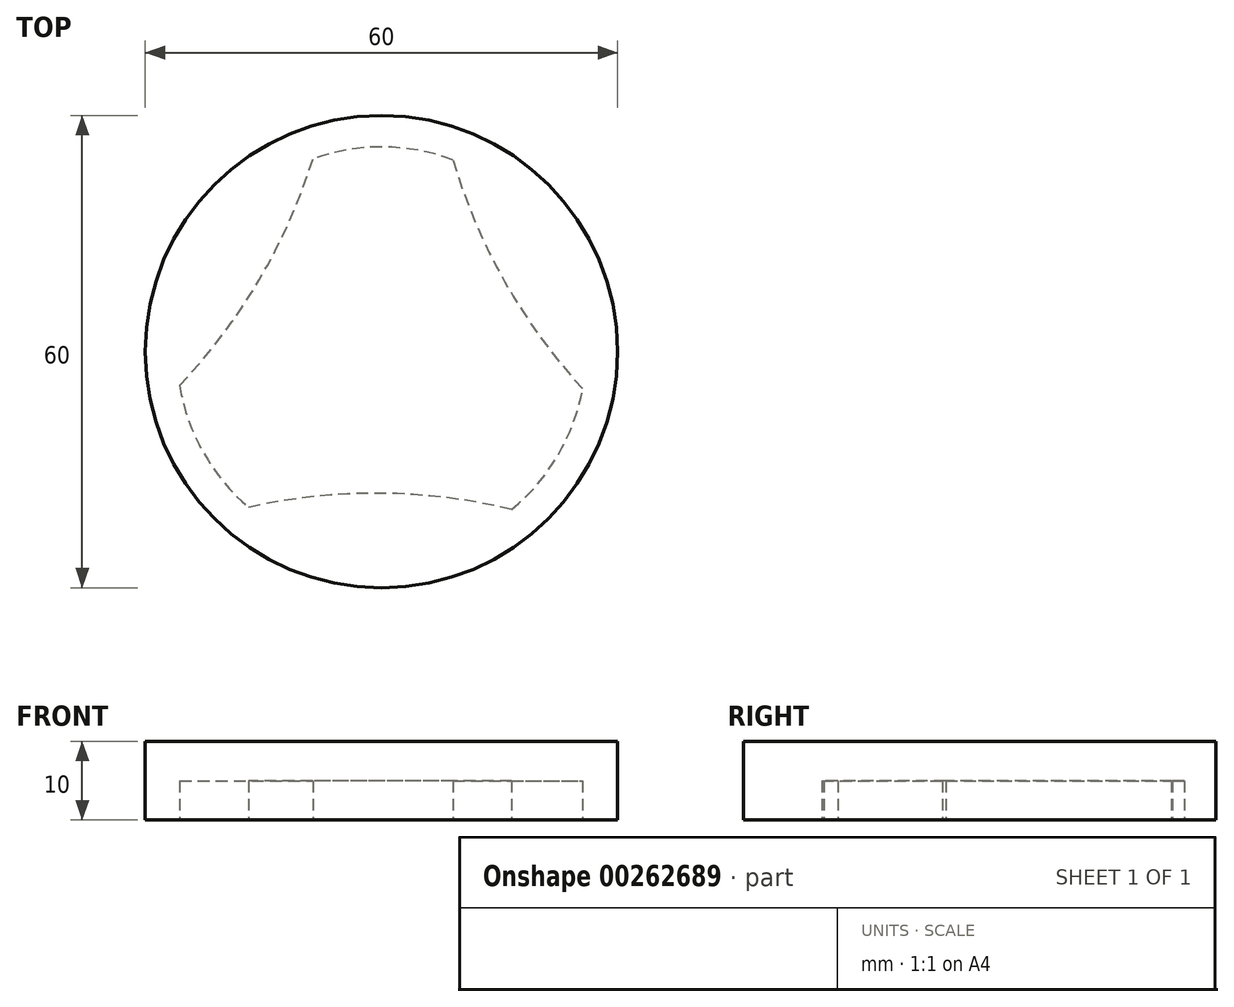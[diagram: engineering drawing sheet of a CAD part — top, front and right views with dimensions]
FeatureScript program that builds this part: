
annotation { "Feature Type Name" : "Feature", "Feature Type Description" : "" }
export const myFeature = defineFeature(function(context is Context, id is Id, definition is map)
    precondition{}
    {
        {
            var Q0;
            Q0=qCreatedBy(makeId("Top.planeOp"),FACE);
            var sketch = newSketch(context, id + "F0", { "sketchPlane" : qUnion([Q0])});
            skCircle(sketch, "E0", {"center": v(0, 0) * mm, "radius": 30 * mm});
            skSolve(sketch);
        }
        {
            var Q0;
            Q0 = qSketchRegion(id + "F0", true);
            extrude(context, id + "F1", {"entities" : qUnion([Q0]), "depth" : 10 * mm});
        }
        {
            var Q0;
            Q0=qCreatedBy(makeId("Top.planeOp"),FACE);
            var sketch = newSketch(context, id + "F2", { "sketchPlane" : qUnion([Q0])});
            skCircle(sketch, "E1", {"center": v(0, 0) * mm, "radius": 26 * mm, "construction": true});
            skLineSegment(sketch, "E2", {"start": v(0, 0) * mm, "end": v(9.09, 24.36) * mm, "construction": true});
            skLineSegment(sketch, "E3", {"start": v(0, 0) * mm, "end": v(22.62, 12.82) * mm, "construction": true});
            skLineSegment(sketch, "E4", {"start": v(0, 0) * mm, "end": v(25.57, -4.72) * mm, "construction": true});
            skLineSegment(sketch, "E5", {"start": v(0, 0) * mm, "end": v(16.55, -20.05) * mm, "construction": true});
            skLineSegment(sketch, "E6", {"start": v(0, 0) * mm, "end": v(-0.2, -26) * mm, "construction": true});
            skLineSegment(sketch, "E7", {"start": v(0, 0) * mm, "end": v(-16.87, -19.78) * mm, "construction": true});
            skLineSegment(sketch, "E8", {"start": v(0, 0) * mm, "end": v(-25.64, -4.31) * mm, "construction": true});
            skLineSegment(sketch, "E9", {"start": v(0, 0) * mm, "end": v(-22.41, 13.18) * mm, "construction": true});
            skLineSegment(sketch, "E10", {"start": v(0, 0) * mm, "end": v(-8.7, 24.5) * mm, "construction": true});
            skArc(sketch, "E11", {"start": v(9.09, 24.36) * mm, "mid": v(0.2, 26) * mm, "end": v(-8.7, 24.5) * mm});
            skArc(sketch, "E12", {"start": v(16.55, -20.05) * mm, "mid": v(22.41, -13.18) * mm, "end": v(25.57, -4.72) * mm});
            skArc(sketch, "E13", {"start": v(-25.64, -4.31) * mm, "mid": v(-22.62, -12.82) * mm, "end": v(-16.87, -19.78) * mm});
            skArc(sketch, "E14", {"start": v(-25.64, -4.31) * mm, "mid": v(-15.52, 9.12) * mm, "end": v(-8.7, 24.5) * mm});
            skArc(sketch, "E15", {"start": v(9.09, 24.36) * mm, "mid": v(15.66, 8.88) * mm, "end": v(25.57, -4.72) * mm});
            skArc(sketch, "E16", {"start": v(16.55, -20.05) * mm, "mid": v(-0.14, -18) * mm, "end": v(-16.87, -19.78) * mm});
            skSolve(sketch);
        }
        {
            var Q0;
            Q0 = qSketchRegion(id + "F2", true);
            extrude(context, id + "F3", {"entities" : qUnion([Q0]), "operationType" : NewBodyOperationType.REMOVE, "depth" : 5 * mm});
        }
    });
